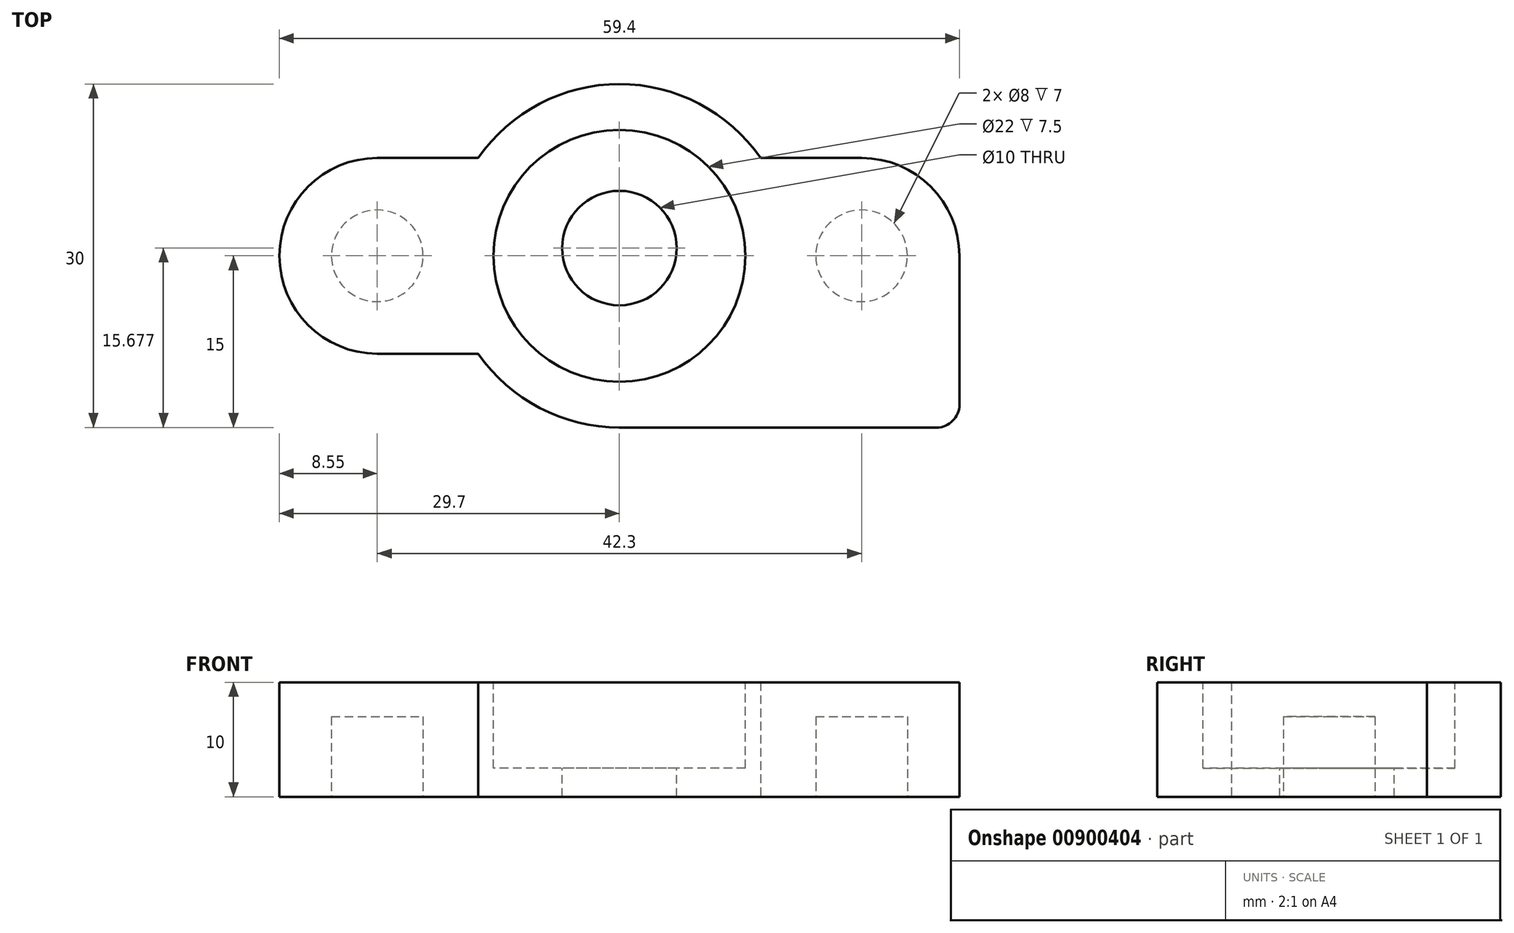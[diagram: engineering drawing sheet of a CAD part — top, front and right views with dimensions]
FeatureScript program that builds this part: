
annotation { "Feature Type Name" : "Feature", "Feature Type Description" : "" }
export const myFeature = defineFeature(function(context is Context, id is Id, definition is map)
    precondition{}
    {
        {
            var Q0;
            Q0=qCreatedBy(makeId("Top.planeOp"),FACE);
            var sketch = newSketch(context, id + "F0", { "sketchPlane" : qUnion([Q0])});
            skPoint(sketch, "E0.middle", {"position": v(0, 0) * mm});
            skArc(sketch, "E1", {"start": v(29.7, 0) * mm, "mid": v(27.2, 6.04) * mm, "end": v(21.15, 8.55) * mm});
            skArc(sketch, "E2", {"start": v(-21.15, 8.55) * mm, "mid": v(-29.7, 0) * mm, "end": v(-21.15, -8.55) * mm});
            skArc(sketch, "E3", {"start": v(12.33, 8.55) * mm, "mid": v(0, 15) * mm, "end": v(-12.33, 8.55) * mm});
            skLineSegment(sketch, "E4", {"start": v(-21.15, 8.55) * mm, "end": v(-12.33, 8.55) * mm});
            skLineSegment(sketch, "E5", {"start": v(12.33, 8.55) * mm, "end": v(21.15, 8.55) * mm});
            skLineSegment(sketch, "E6", {"start": v(-21.15, -8.55) * mm, "end": v(-12.33, -8.55) * mm});
            skArc(sketch, "E7.trimOffspring", {"start": v(-12.33, -8.55) * mm, "mid": v(-6.96, -13.29) * mm, "end": v(0, -15) * mm});
            skPoint(sketch, "E0.bottom.end.orphan", {"position": v(-21.15, 21.6) * mm});
            skPoint(sketch, "E8.orphan", {"position": v(21.15, 21.6) * mm});
            skPoint(sketch, "E0.top.start.orphan", {"position": v(21.15, -21.6) * mm});
            skPoint(sketch, "E9.orphan", {"position": v(-21.15, -21.6) * mm});
            skLineSegment(sketch, "E10", {"start": v(0, -15) * mm, "end": v(29.7, -15) * mm});
            skPoint(sketch, "E10.endSnap0", {"position": v(29.7, 0) * mm});
            skLineSegment(sketch, "E11", {"start": v(29.7, -15) * mm, "end": v(29.7, 0) * mm});
            skSolve(sketch);
        }
        {
            var Q0;
            Q0 = qSketchRegion(id + "F0", true);
            extrude(context, id + "F1", {"entities" : qUnion([Q0]), "depth" : 10 * mm, "offsetDistance" : 25 * mm});
        }
        {
            var Q0;
            Q0=makeQuery(id+"F1.opExtrude","CAP_FACE",FACE,{"disambiguationData":[OSD([sQuery(id+"F0.wireOp",EDGE,"E1"),sQuery(id+"F0.wireOp",EDGE,"E2"),sQuery(id+"F0.wireOp",EDGE,"E3"),sQuery(id+"F0.wireOp",EDGE,"E4"),sQuery(id+"F0.wireOp",EDGE,"E5"),sQuery(id+"F0.wireOp",EDGE,"E6"),sQuery(id+"F0.wireOp",EDGE,"cee39a7c-e6e2-45f2-9597-b2fe7dd0f8be.trimOffspring"),sQuery(id+"F0.wireOp",EDGE,"E7.trimOffspring")])],"isStart":false});
            var sketch = newSketch(context, id + "F2", { "sketchPlane" : qUnion([Q0])});
            skCircle(sketch, "E12", {"center": v(0, 0) * mm, "radius": 11 * mm});
            skSolve(sketch);
        }
        {
            var Q0;
            Q0 = qSketchRegion(id + "F2", true);
            extrude(context, id + "F3", {"entities" : qUnion([Q0]), "operationType" : NewBodyOperationType.REMOVE, "oppositeDirection" : true, "depth" : 7.5 * mm, "offsetDistance" : 25 * mm});
        }
        {
            var Q0;
            Q0=makeQuery(id+"F1.opExtrude","CAP_FACE",FACE,{"disambiguationData":[OSD([sQuery(id+"F0.wireOp",EDGE,"E1"),sQuery(id+"F0.wireOp",EDGE,"E2"),sQuery(id+"F0.wireOp",EDGE,"E3"),sQuery(id+"F0.wireOp",EDGE,"E4"),sQuery(id+"F0.wireOp",EDGE,"E5"),sQuery(id+"F0.wireOp",EDGE,"E6"),sQuery(id+"F0.wireOp",EDGE,"cee39a7c-e6e2-45f2-9597-b2fe7dd0f8be.trimOffspring"),sQuery(id+"F0.wireOp",EDGE,"E7.trimOffspring")])],"isStart":true});
            var sketch = newSketch(context, id + "F4", { "sketchPlane" : qUnion([Q0])});
            skCircle(sketch, "E13", {"center": v(-21.15, 0) * mm, "radius": 4 * mm});
            skCircle(sketch, "E14", {"center": v(21.15, 0) * mm, "radius": 4 * mm});
            skSolve(sketch);
        }
        {
            var Q0;
            Q0 = qSketchRegion(id + "FbdQ1F48fTcBCxs_1", true);
            var Q1;
            Q1=makeQuery(id+"F4.imprint","IMPRINT",FACE,{"disambiguationData":[TD([[makeQuery(id+"F4.imprint","IMPRINT",EDGE,{"derivedFrom":sQuery(id+"F4.wireOp",EDGE,"E13")}),1.0]])]});
            var Q2;
            Q2=makeQuery(id+"F4.imprint","IMPRINT",FACE,{"disambiguationData":[TD([[makeQuery(id+"F4.imprint","IMPRINT",EDGE,{"derivedFrom":sQuery(id+"F4.wireOp",EDGE,"E14")}),1.0]])]});
            extrude(context, id + "F5", {"entities" : qUnion([Q0, Q1, Q2]), "operationType" : NewBodyOperationType.REMOVE, "oppositeDirection" : true, "depth" : 7 * mm, "offsetDistance" : 25 * mm});
        }
        {
            var Q0;
            Q0=makeQuery(id+"F3.boolean.opBoolean","COPY",FACE,{"derivedFrom":makeQuery(id+"F3.opExtrude","CAP_FACE",FACE,{"disambiguationData":[OSD([sQuery(id+"F2.wireOp",EDGE,"E12")])],"isStart":false})});
            var sketch = newSketch(context, id + "F6", { "sketchPlane" : qUnion([Q0])});
            skCircle(sketch, "E15", {"center": v(0, 0.68) * mm, "radius": 5 * mm});
            skSolve(sketch);
        }
        {
            var Q0;
            Q0 = qSketchRegion(id + "F05wcR2b1KYWTuP_1", true);
            var Q1;
            Q1=makeQuery(id+"F6.imprint","IMPRINT",FACE,{"disambiguationData":[TD([[makeQuery(id+"F6.imprint","IMPRINT",EDGE,{"derivedFrom":sQuery(id+"F6.wireOp",EDGE,"E15")}),1.0]])]});
            extrude(context, id + "F7", {"entities" : qUnion([Q0, Q1]), "operationType" : NewBodyOperationType.REMOVE, "oppositeDirection" : true, "depth" : 25 * mm, "offsetDistance" : 25 * mm});
        }
        {
            var Q0;
            Q0=makeQuery(id+"F1.opExtrude","SWEPT_EDGE",EDGE,{"disambiguationData":[OSD([sQuery(id+"F0.wireOp",EDGE,"E10"),sQuery(id+"F0.wireOp",EDGE,"E11")])]});
            fillet(context, id + "F8", {"entities" : qUnion([Q0]), "radius" : 2 * mm, "tangentPropagation" : true, "allowEdgeOverflow" : false});
        }
    });
